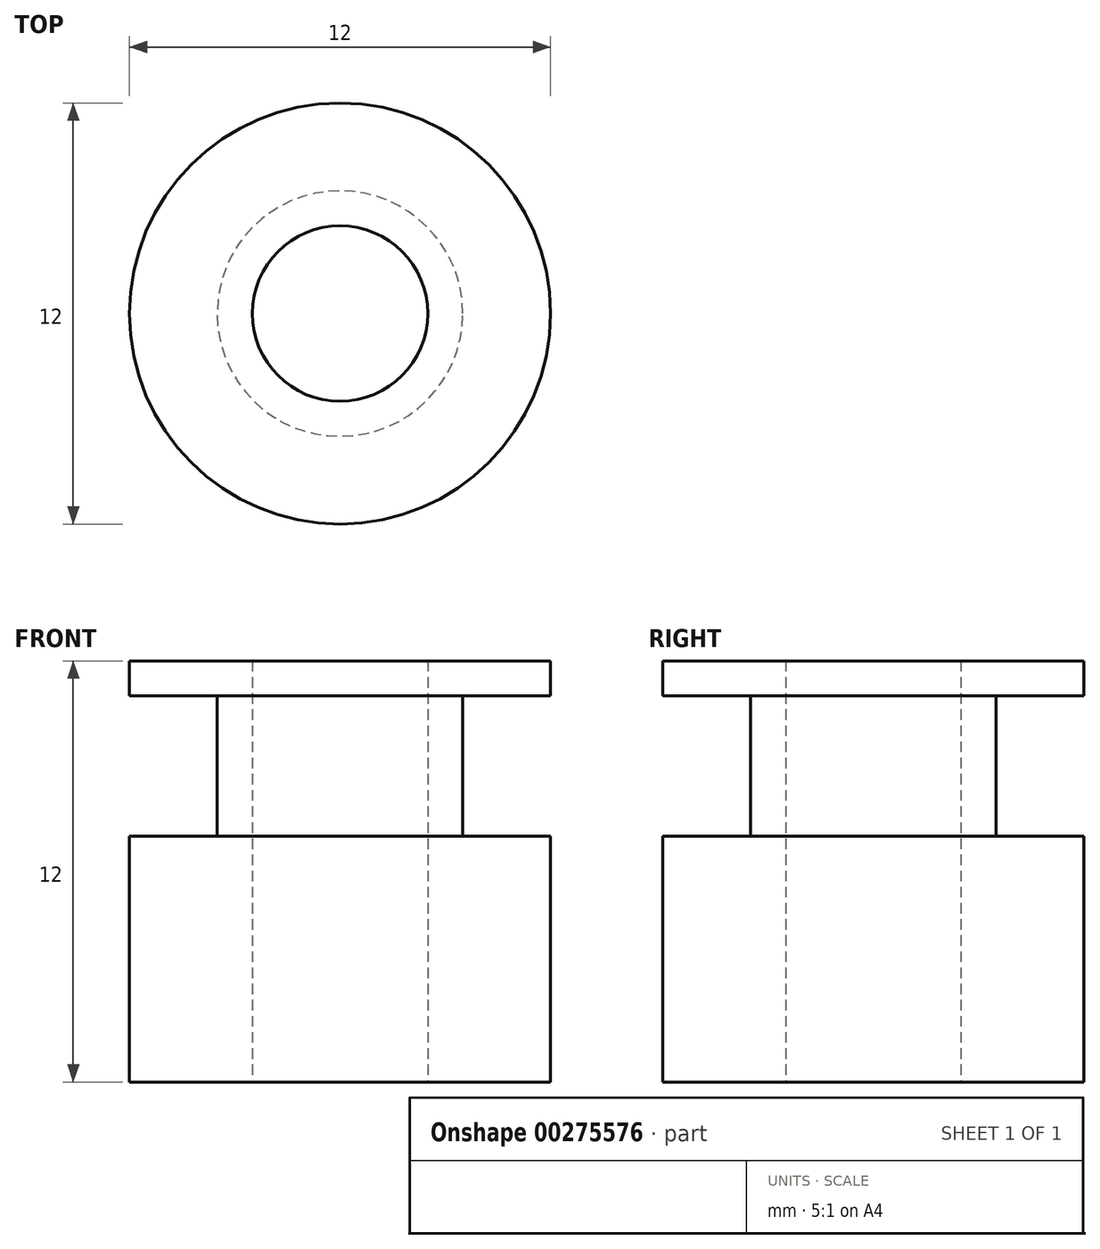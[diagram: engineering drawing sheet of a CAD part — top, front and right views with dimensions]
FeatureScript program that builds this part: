
annotation { "Feature Type Name" : "Feature", "Feature Type Description" : "" }
export const myFeature = defineFeature(function(context is Context, id is Id, definition is map)
    precondition{}
    {
        {
            var Q0;
            Q0=qCreatedBy(makeId("Front.planeOp"),FACE);
            var sketch = newSketch(context, id + "F0", { "sketchPlane" : qUnion([Q0])});
            skLineSegment(sketch, "E0", {"start": v(0, 0) * mm, "end": v(0, 12) * mm, "construction": true});
            skLineSegment(sketch, "E1", {"start": v(2.5, 0) * mm, "end": v(6, 0) * mm});
            skLineSegment(sketch, "E2", {"start": v(6, 0) * mm, "end": v(6, 7) * mm});
            skLineSegment(sketch, "E3", {"start": v(6, 7) * mm, "end": v(3.5, 7) * mm});
            skLineSegment(sketch, "E4", {"start": v(3.5, 7) * mm, "end": v(3.5, 11) * mm});
            skLineSegment(sketch, "E5", {"start": v(3.5, 11) * mm, "end": v(6, 11) * mm});
            skLineSegment(sketch, "E6", {"start": v(6, 11) * mm, "end": v(6, 12) * mm});
            skLineSegment(sketch, "E7", {"start": v(6, 12) * mm, "end": v(2.5, 12) * mm});
            skLineSegment(sketch, "E8", {"start": v(2.5, 12) * mm, "end": v(2.5, 0) * mm});
            skSolve(sketch);
        }
        {
            var Q0;
            Q0 = qSketchRegion(id + "F0", true);
            var Q1;
            Q1=sQuery(id+"F0.wireOp",EDGE,"E0");
            revolve(context, id + "F1", {"entities" : qUnion([Q0]), "axis" : qUnion([Q1]), "revolveType" : RevolveType.FULL});
        }
    });
